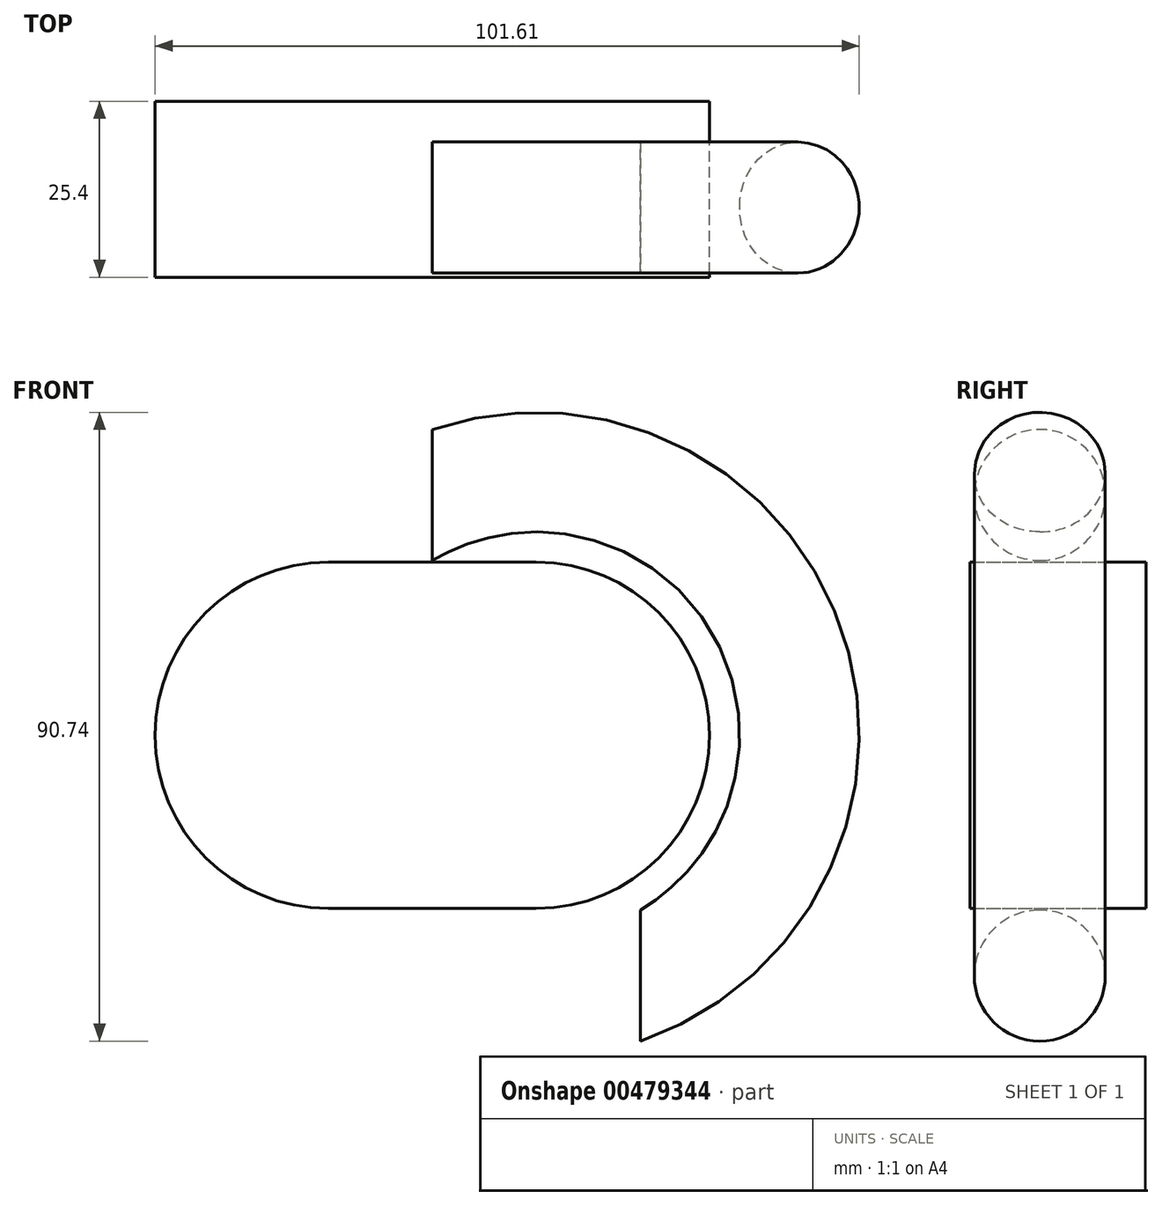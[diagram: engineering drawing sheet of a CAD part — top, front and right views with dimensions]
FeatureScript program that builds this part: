
annotation { "Feature Type Name" : "Feature", "Feature Type Description" : "" }
export const myFeature = defineFeature(function(context is Context, id is Id, definition is map)
    precondition{}
    {
        {
            var Q0;
            Q0=qCreatedBy(makeId("Front.planeOp"),FACE);
            var sketch = newSketch(context, id + "F0", { "sketchPlane" : qUnion([Q0])});
            skLineSegment(sketch, "E0.bottom", {"start": v(0, -25) * mm, "end": v(-15, -25) * mm});
            skLineSegment(sketch, "E0.top", {"start": v(0, 25) * mm, "end": v(-15, 25) * mm});
            skPoint(sketch, "E1.end.orphan", {"position": v(-40, 0) * mm});
            skArc(sketch, "E2", {"start": v(-15, 25) * mm, "mid": v(-40, 0) * mm, "end": v(-15, -25) * mm});
            skLineSegment(sketch, "E3.bottom", {"start": v(0, -25) * mm, "end": v(15, -25) * mm});
            skLineSegment(sketch, "E3.top", {"start": v(0, 25) * mm, "end": v(15, 25) * mm});
            skArc(sketch, "E4", {"start": v(15, -25) * mm, "mid": v(40, 0) * mm, "end": v(15, 25) * mm});
            skPoint(sketch, "E5.orphan", {"position": v(-40, 25) * mm});
            skPoint(sketch, "E6.orphan", {"position": v(40, -25) * mm});
            skPoint(sketch, "E7.end.orphan", {"position": v(0, 25) * mm});
            skPoint(sketch, "E7.start.orphan", {"position": v(0, 0) * mm});
            skPoint(sketch, "E8.start.orphan", {"position": v(40, 0) * mm});
            skPoint(sketch, "E9.orphan", {"position": v(40, 25) * mm});
            skSolve(sketch);
        }
        {
            var Q0;
            Q0=makeQuery(id+"F0.imprint","IMPRINT",FACE,{"disambiguationData":[TD([[makeQuery(id+"F0.imprint","IMPRINT",EDGE,{"derivedFrom":sQuery(id+"F0.wireOp",EDGE,"E0.bottom")}),-1.0]])]});
            extrude(context, id + "F1", {"entities" : qUnion([Q0]), "depth" : 25.4 * mm, "offsetDistance" : 25.4 * mm});
        }
        {
            var Q0;
            Q0=qCreatedBy(makeId("Right.planeOp"),FACE);
            var sketch = newSketch(context, id + "F2", { "sketchPlane" : qUnion([Q0])});
            skCircle(sketch, "E10", {"center": v(-15.35, 34.68) * mm, "radius": 9.45 * mm});
            skSolve(sketch);
        }
        {
            var Q0;
            Q0=makeQuery(id+"F2.imprint","IMPRINT",FACE,{"disambiguationData":[TD([[makeQuery(id+"F2.imprint","IMPRINT",EDGE,{"derivedFrom":sQuery(id+"F2.wireOp",EDGE,"E10")}),1.0]])]});
            var Q1;
            Q1=makeQuery(id+"F1.opExtrude","CAP_EDGE",EDGE,{"disambiguationData":[OSD([sQuery(id+"F0.wireOp",EDGE,"E4")])],"isStart":false});
            sweep(context, id + "F3", {"profiles" : qUnion([Q0]), "path" : qUnion([Q1])});
        }
    });
